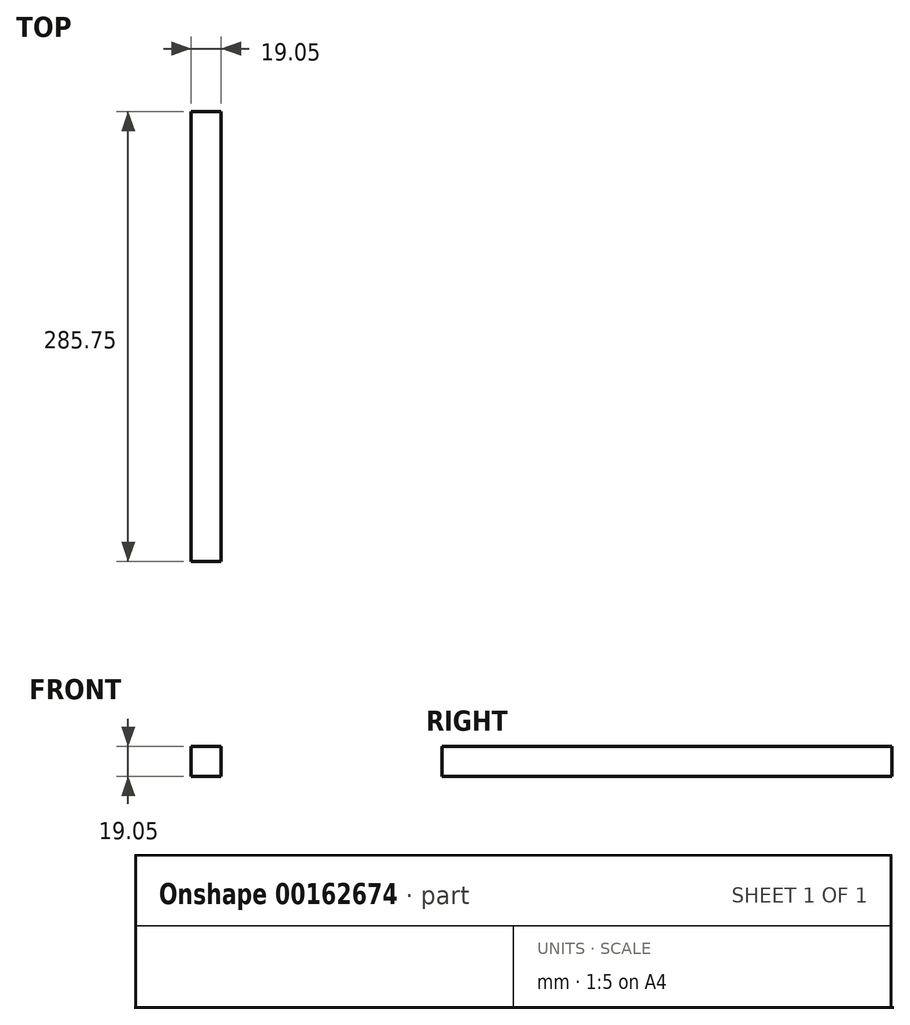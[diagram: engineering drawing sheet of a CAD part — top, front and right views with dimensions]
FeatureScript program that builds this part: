
annotation { "Feature Type Name" : "Feature", "Feature Type Description" : "" }
export const myFeature = defineFeature(function(context is Context, id is Id, definition is map)
    precondition{}
    {
        {
            var Q0;
            Q0=qCreatedBy(makeId("Right.planeOp"),FACE);
            var sketch = newSketch(context, id + "F0", { "sketchPlane" : qUnion([Q0])});
            skLineSegment(sketch, "E0.bottom", {"start": v(-144.02, 52.64) * mm, "end": v(141.73, 52.64) * mm});
            skLineSegment(sketch, "E0.top", {"start": v(-144.02, 33.59) * mm, "end": v(141.73, 33.59) * mm});
            skLineSegment(sketch, "E0.left", {"start": v(-144.02, 52.64) * mm, "end": v(-144.02, 33.59) * mm});
            skLineSegment(sketch, "E0.right", {"start": v(141.73, 52.64) * mm, "end": v(141.73, 33.59) * mm});
            skSolve(sketch);
        }
        {
            var Q0;
            Q0 = qSketchRegion(id + "F0", true);
            extrude(context, id + "F1", {"entities" : qUnion([Q0]), "depth" : 19.05 * mm});
        }
    });
